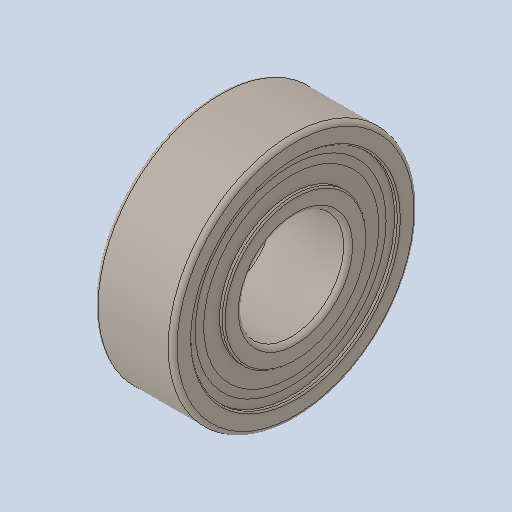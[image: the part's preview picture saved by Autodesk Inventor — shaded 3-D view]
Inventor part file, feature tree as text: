
AUTODESK INVENTOR PART (.ipt)
format: ipt  version: 2023.4 (Build 274418000, 418)  size: 234,496 bytes
history: native  units: in
note: dims shown in document units (in); Inventor stores cm internally (conversion verified against a paired STEP export)
features: revolve x1
ambient origin geometry x8: Origin, YZ Plane, XZ Plane, XY Plane, X Axis, Y Axis, Z Axis, Center Point
bodies: Solid1 (feature_tree)
feature tree (1):
  revolve  "Revolve1"  [1 undecoded]
note: 1 required parameter value undecoded (feature->parameter linkage not recoverable at this tier; creation-order binding heuristic only, values carry confidence <= 0.55)
